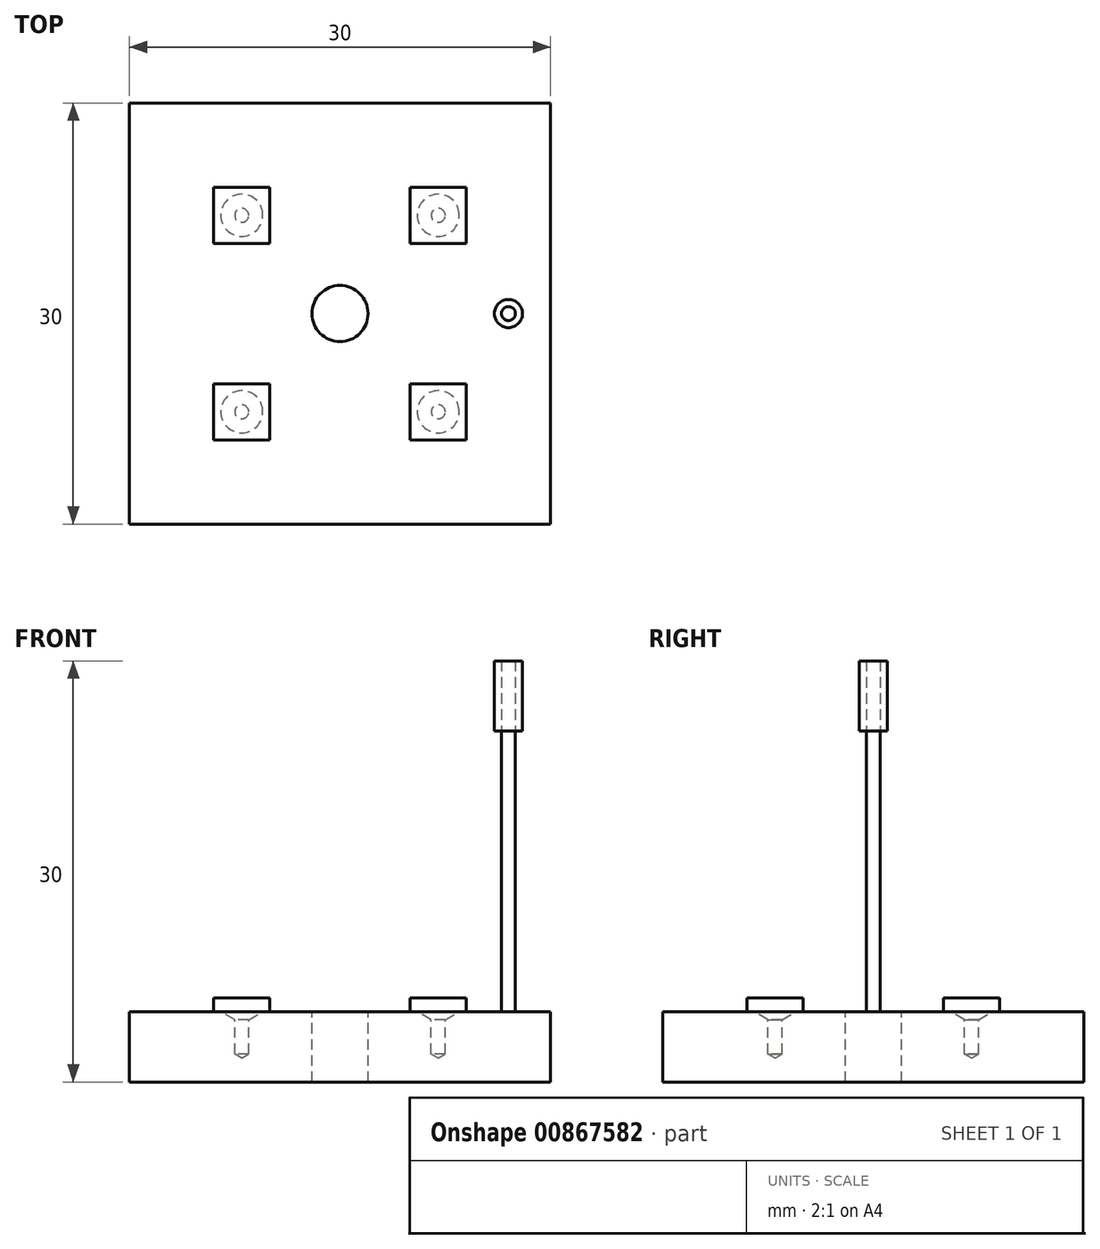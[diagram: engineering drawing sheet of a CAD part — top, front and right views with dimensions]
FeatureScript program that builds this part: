
annotation { "Feature Type Name" : "Feature", "Feature Type Description" : "" }
export const myFeature = defineFeature(function(context is Context, id is Id, definition is map)
    precondition{}
    {
        {
            var Q0;
            Q0=qCreatedBy(makeId("Top.planeOp"),FACE);
            var sketch = newSketch(context, id + "F0", { "sketchPlane" : qUnion([Q0])});
            skLineSegment(sketch, "E0.bottom", {"start": v(15, -15) * mm, "end": v(-15, -15) * mm});
            skLineSegment(sketch, "E0.top", {"start": v(15, 15) * mm, "end": v(-15, 15) * mm});
            skLineSegment(sketch, "E0.left", {"start": v(15, -15) * mm, "end": v(15, 15) * mm});
            skLineSegment(sketch, "E0.right", {"start": v(-15, -15) * mm, "end": v(-15, 15) * mm});
            skPoint(sketch, "E0.middle", {"position": v(0, 0) * mm});
            skSolve(sketch);
        }
        {
            var Q0;
            Q0 = qSketchRegion(id + "F0", true);
            extrude(context, id + "F1", {"entities" : qUnion([Q0]), "depth" : 5 * mm, "offsetDistance" : 25 * mm});
        }
        {
            var Q0;
            Q0=makeQuery(id+"F1.opExtrude","CAP_FACE",FACE,{"disambiguationData":[OSD([sQuery(id+"F0.wireOp",EDGE,"E0.bottom"),sQuery(id+"F0.wireOp",EDGE,"E0.top"),sQuery(id+"F0.wireOp",EDGE,"E0.left"),sQuery(id+"F0.wireOp",EDGE,"E0.right")])],"isStart":false});
            var sketch = newSketch(context, id + "F2", { "sketchPlane" : qUnion([Q0])});
            skPoint(sketch, "E1", {"position": v(-7, 7) * mm});
            skPoint(sketch, "E2.MirrorP", {"position": v(7, 7) * mm});
            skPoint(sketch, "E3.MirrorP", {"position": v(-7, -7) * mm});
            skPoint(sketch, "E4.MirrorP", {"position": v(7, -7) * mm});
            skSolve(sketch);
        }
        {
            var Q0;
            Q0=sQuery(id+"F2.wireOp",VERTEX,"E1");
            var Q1;
            Q1=sQuery(id+"F2.wireOp",VERTEX,"E3.MirrorP");
            var Q2;
            Q2=sQuery(id+"F2.wireOp",VERTEX,"E4.MirrorP");
            var Q3;
            Q3=sQuery(id+"F2.wireOp",VERTEX,"E2.MirrorP");
            var Q4;
            Q4=makeQuery(id+"F1.opExtrude","SWEPT_BODY",BODY,{"disambiguationData":[OSD([sQuery(id+"F0.wireOp",EDGE,"E0.bottom"),sQuery(id+"F0.wireOp",EDGE,"E0.top"),sQuery(id+"F0.wireOp",EDGE,"E0.left"),sQuery(id+"F0.wireOp",EDGE,"E0.right")])]});
            hole(context, id + "F3", {"style" : HoleStyle.C_SINK, "endStyle" : HoleEndStyle.BLIND, "holeDiameter" : 1 * mm, "cSinkDiameter" : 3 * mm, "cSinkAngle" : 120 * degree, "majorDiameter" : 5 * mm, "holeDepth" : 3 * mm, "isTappedThrough" : true, "tappedDepth" : 12 * mm, "tapClearance" : 3, "startFromSketch" : true, "locations" : qUnion([Q0, Q1, Q2, Q3]), "scope" : qUnion([Q4])});
        }
        {
            var Q0;
            Q0=qCreatedBy(makeId("Top.planeOp"),FACE);
            cPlane(context, id + "F4", {"entities" : qUnion([Q0]), "cplaneType" : CPlaneType.OFFSET, "offset" : 6 * mm, "width" : 150 * mm, "height" : 150 * mm});
        }
        {
            var Q0;
            Q0=qCreatedBy(id+"F4.planeOp",FACE);
            var sketch = newSketch(context, id + "F5", { "sketchPlane" : qUnion([Q0])});
            skLineSegment(sketch, "E5.bottom", {"start": v(-5, 5) * mm, "end": v(-9, 5) * mm});
            skLineSegment(sketch, "E5.top", {"start": v(-5, 9) * mm, "end": v(-9, 9) * mm});
            skLineSegment(sketch, "E5.left", {"start": v(-5, 5) * mm, "end": v(-5, 9) * mm});
            skLineSegment(sketch, "E5.right", {"start": v(-9, 5) * mm, "end": v(-9, 9) * mm});
            skPoint(sketch, "E5.middle", {"position": v(-7, 7) * mm});
            skSolve(sketch);
        }
        {
            var Q0;
            Q0 = qSketchRegion(id + "F5", true);
            var Q1;
            Q1=makeQuery(id+"F1.opExtrude","CAP_FACE",FACE,{"disambiguationData":[OSD([sQuery(id+"F0.wireOp",EDGE,"E0.bottom"),sQuery(id+"F0.wireOp",EDGE,"E0.top"),sQuery(id+"F0.wireOp",EDGE,"E0.left"),sQuery(id+"F0.wireOp",EDGE,"E0.right")])],"isStart":true});
            extrude(context, id + "F6", {"entities" : qUnion([Q0]), "endBound" : BoundingType.UP_TO_SURFACE, "oppositeDirection" : true, "depth" : 0.5 * mm, "endBoundEntityFace" : qUnion([Q1]), "offsetDistance" : 25 * mm});
        }
        {
            var Q0;
            Q0=makeQuery(id+"F6.opExtrude","SWEPT_BODY",BODY,{"disambiguationData":[OSD([sQuery(id+"F5.wireOp",EDGE,"E5.bottom"),sQuery(id+"F5.wireOp",EDGE,"E5.top"),sQuery(id+"F5.wireOp",EDGE,"E5.left"),sQuery(id+"F5.wireOp",EDGE,"E5.right")])]});
            var Q1;
            Q1=qCreatedBy(makeId("Right.planeOp"),FACE);
            mirror(context, id + "F7", {"entities" : qUnion([Q0]), "mirrorPlane" : qUnion([Q1])});
        }
        {
            var Q0;
            Q0=makeQuery(id+"F6.opExtrude","SWEPT_BODY",BODY,{"disambiguationData":[OSD([sQuery(id+"F5.wireOp",EDGE,"E5.bottom"),sQuery(id+"F5.wireOp",EDGE,"E5.top"),sQuery(id+"F5.wireOp",EDGE,"E5.left"),sQuery(id+"F5.wireOp",EDGE,"E5.right")])]});
            var Q1;
            Q1=makeQuery(id+"F7.opPattern","COPY",BODY,{"derivedFrom":makeQuery(id+"F6.opExtrude","SWEPT_BODY",BODY,{"disambiguationData":[OSD([sQuery(id+"F5.wireOp",EDGE,"E5.bottom"),sQuery(id+"F5.wireOp",EDGE,"E5.top"),sQuery(id+"F5.wireOp",EDGE,"E5.left"),sQuery(id+"F5.wireOp",EDGE,"E5.right")])]}),"instanceName":"1"});
            var Q2;
            Q2=qCreatedBy(makeId("Front.planeOp"),FACE);
            mirror(context, id + "F8", {"entities" : qUnion([Q0, Q1]), "mirrorPlane" : qUnion([Q2])});
        }
        {
            var Q0;
            Q0=makeQuery(id+"F1.opExtrude","SWEPT_BODY",BODY,{"disambiguationData":[OSD([sQuery(id+"F0.wireOp",EDGE,"E0.bottom"),sQuery(id+"F0.wireOp",EDGE,"E0.top"),sQuery(id+"F0.wireOp",EDGE,"E0.left"),sQuery(id+"F0.wireOp",EDGE,"E0.right")])]});
            var Q1;
            Q1=makeQuery(id+"F6.opExtrude","SWEPT_BODY",BODY,{"disambiguationData":[OSD([sQuery(id+"F5.wireOp",EDGE,"E5.bottom"),sQuery(id+"F5.wireOp",EDGE,"E5.top"),sQuery(id+"F5.wireOp",EDGE,"E5.left"),sQuery(id+"F5.wireOp",EDGE,"E5.right")])]});
            var Q2;
            Q2=makeQuery(id+"F8.opPattern","COPY",BODY,{"derivedFrom":makeQuery(id+"F6.opExtrude","SWEPT_BODY",BODY,{"disambiguationData":[OSD([sQuery(id+"F5.wireOp",EDGE,"E5.bottom"),sQuery(id+"F5.wireOp",EDGE,"E5.top"),sQuery(id+"F5.wireOp",EDGE,"E5.left"),sQuery(id+"F5.wireOp",EDGE,"E5.right")])]}),"instanceName":"1"});
            var Q3;
            Q3=makeQuery(id+"F8.opPattern","COPY",BODY,{"derivedFrom":makeQuery(id+"F7.opPattern","COPY",BODY,{"derivedFrom":makeQuery(id+"F6.opExtrude","SWEPT_BODY",BODY,{"disambiguationData":[OSD([sQuery(id+"F5.wireOp",EDGE,"E5.bottom"),sQuery(id+"F5.wireOp",EDGE,"E5.top"),sQuery(id+"F5.wireOp",EDGE,"E5.left"),sQuery(id+"F5.wireOp",EDGE,"E5.right")])]}),"instanceName":"1"}),"instanceName":"1"});
            var Q4;
            Q4=makeQuery(id+"F7.opPattern","COPY",BODY,{"derivedFrom":makeQuery(id+"F6.opExtrude","SWEPT_BODY",BODY,{"disambiguationData":[OSD([sQuery(id+"F5.wireOp",EDGE,"E5.bottom"),sQuery(id+"F5.wireOp",EDGE,"E5.top"),sQuery(id+"F5.wireOp",EDGE,"E5.left"),sQuery(id+"F5.wireOp",EDGE,"E5.right")])]}),"instanceName":"1"});
            booleanBodies(context, id + "F9", {"operationType" : BooleanOperationType.SUBTRACTION, "tools" : qUnion([Q0]), "targets" : qUnion([Q1, Q2, Q3, Q4]), "keepTools" : true});
        }
        {
            var Q0;
            Q0=makeQuery(id+"F1.opExtrude","CAP_FACE",FACE,{"disambiguationData":[OSD([sQuery(id+"F0.wireOp",EDGE,"E0.bottom"),sQuery(id+"F0.wireOp",EDGE,"E0.top"),sQuery(id+"F0.wireOp",EDGE,"E0.left"),sQuery(id+"F0.wireOp",EDGE,"E0.right")])],"isStart":false});
            var sketch = newSketch(context, id + "F10", { "sketchPlane" : qUnion([Q0])});
            skCircle(sketch, "E6", {"center": v(12, 0) * mm, "radius": 0.5 * mm});
            skSolve(sketch);
        }
        {
            var Q0;
            Q0 = qSketchRegion(id + "F10", true);
            extrude(context, id + "F11", {"entities" : qUnion([Q0]), "operationType" : NewBodyOperationType.ADD, "depth" : 25 * mm, "offsetDistance" : 25 * mm});
        }
        {
            var Q0;
            Q0=makeQuery(id+"F11.opExtrude","CAP_FACE",FACE,{"disambiguationData":[OSD([sQuery(id+"F10.wireOp",EDGE,"E6")])],"isStart":false});
            var sketch = newSketch(context, id + "F12", { "sketchPlane" : qUnion([Q0])});
            skCircle(sketch, "E7", {"center": v(12, 0) * mm, "radius": 1 * mm});
            skSolve(sketch);
        }
        {
            var Q0;
            Q0 = qSketchRegion(id + "F12", true);
            extrude(context, id + "F13", {"entities" : qUnion([Q0]), "oppositeDirection" : true, "depth" : 5 * mm, "offsetDistance" : 25 * mm});
        }
        {
            var Q0;
            Q0=makeQuery(id+"F1.opExtrude","SWEPT_BODY",BODY,{"disambiguationData":[OSD([sQuery(id+"F0.wireOp",EDGE,"E0.bottom"),sQuery(id+"F0.wireOp",EDGE,"E0.top"),sQuery(id+"F0.wireOp",EDGE,"E0.left"),sQuery(id+"F0.wireOp",EDGE,"E0.right")])]});
            var Q1;
            Q1=makeQuery(id+"F13.opExtrude","SWEPT_BODY",BODY,{"disambiguationData":[OSD([sQuery(id+"F12.wireOp",EDGE,"E7")])]});
            booleanBodies(context, id + "F14", {"operationType" : BooleanOperationType.SUBTRACTION, "tools" : qUnion([Q0]), "targets" : qUnion([Q1]), "keepTools" : true});
        }
        {
            var Q0;
            Q0=makeQuery(id+"F1.opExtrude","CAP_FACE",FACE,{"disambiguationData":[OSD([sQuery(id+"F0.wireOp",EDGE,"E0.bottom"),sQuery(id+"F0.wireOp",EDGE,"E0.top"),sQuery(id+"F0.wireOp",EDGE,"E0.left"),sQuery(id+"F0.wireOp",EDGE,"E0.right")])],"isStart":false});
            var sketch = newSketch(context, id + "F15", { "sketchPlane" : qUnion([Q0])});
            skCircle(sketch, "E8", {"center": v(0, 0) * mm, "radius": 2 * mm});
            skSolve(sketch);
        }
        {
            var Q0;
            Q0 = qSketchRegion(id + "F15", true);
            var Q1;
            Q1=makeQuery(id+"F1.opExtrude","CAP_FACE",FACE,{"disambiguationData":[OSD([sQuery(id+"F0.wireOp",EDGE,"E0.bottom"),sQuery(id+"F0.wireOp",EDGE,"E0.top"),sQuery(id+"F0.wireOp",EDGE,"E0.left"),sQuery(id+"F0.wireOp",EDGE,"E0.right")])],"isStart":true});
            extrude(context, id + "F16", {"entities" : qUnion([Q0]), "endBound" : BoundingType.UP_TO_SURFACE, "oppositeDirection" : true, "depth" : 25 * mm, "endBoundEntityFace" : qUnion([Q1]), "offsetDistance" : 25 * mm});
        }
        {
            var Q0;
            Q0=makeQuery(id+"F16.opExtrude","SWEPT_BODY",BODY,{"disambiguationData":[OSD([sQuery(id+"F15.wireOp",EDGE,"E8")])]});
            var Q1;
            Q1=makeQuery(id+"F1.opExtrude","SWEPT_BODY",BODY,{"disambiguationData":[OSD([sQuery(id+"F0.wireOp",EDGE,"E0.bottom"),sQuery(id+"F0.wireOp",EDGE,"E0.top"),sQuery(id+"F0.wireOp",EDGE,"E0.left"),sQuery(id+"F0.wireOp",EDGE,"E0.right")])]});
            booleanBodies(context, id + "F17", {"operationType" : BooleanOperationType.SUBTRACTION, "tools" : qUnion([Q0]), "targets" : qUnion([Q1]), "keepTools" : true});
        }
    });
